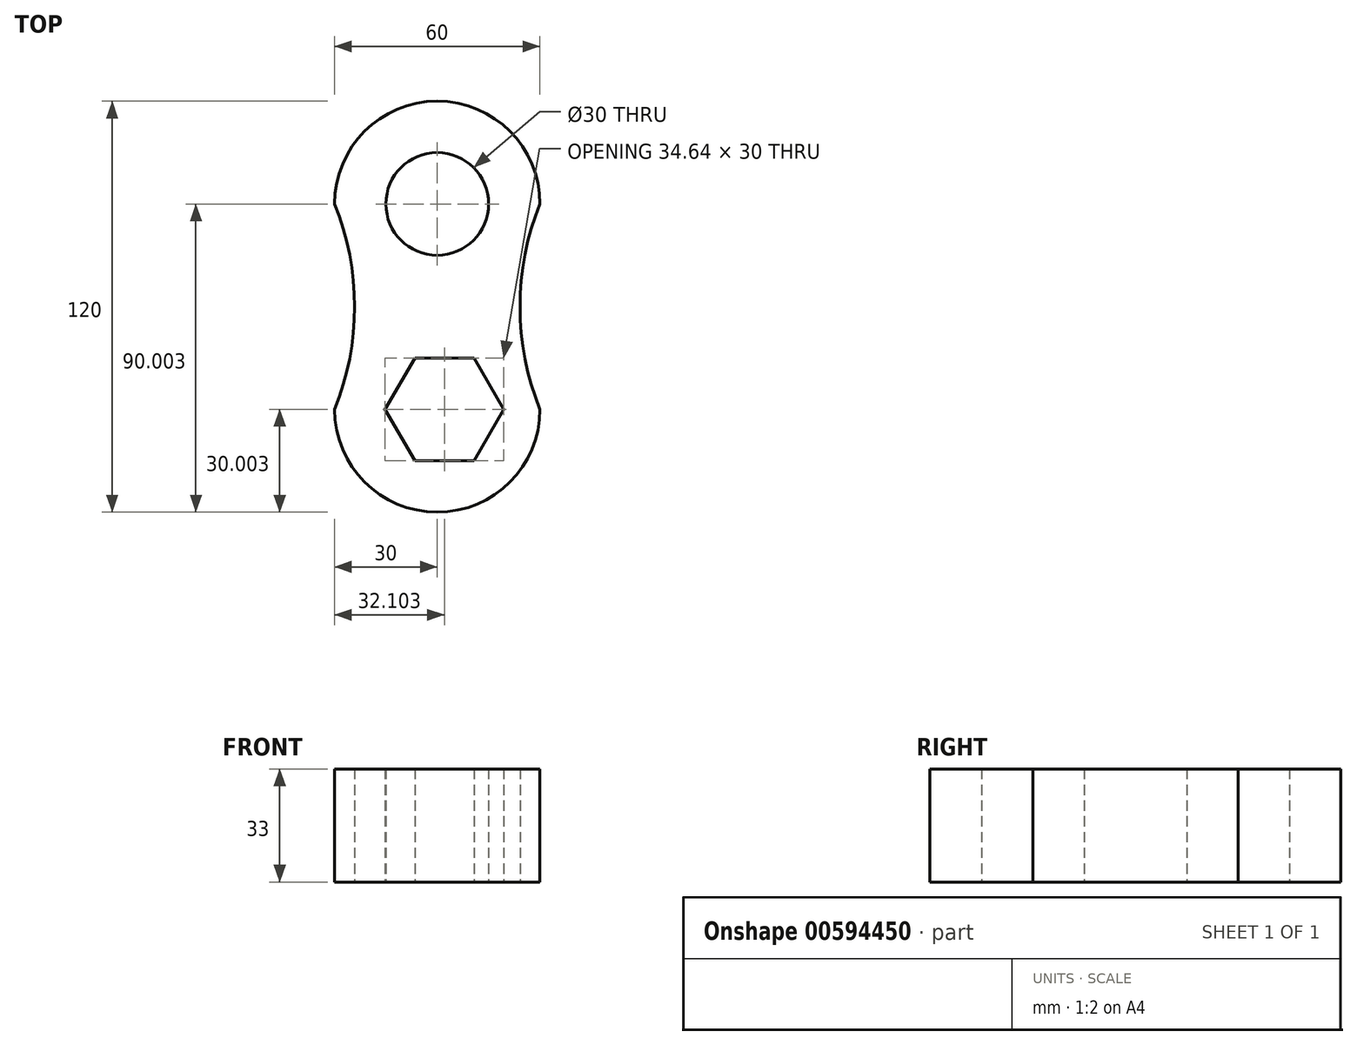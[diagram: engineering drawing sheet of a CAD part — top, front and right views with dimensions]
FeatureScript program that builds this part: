
annotation { "Feature Type Name" : "Feature", "Feature Type Description" : "" }
export const myFeature = defineFeature(function(context is Context, id is Id, definition is map)
    precondition{}
    {
        {
            var Q0;
            Q0=qCreatedBy(makeId("Top.planeOp"),FACE);
            var sketch = newSketch(context, id + "F0", { "sketchPlane" : qUnion([Q0])});
            skArc(sketch, "E0", {"start": v(-15.64, -28.34) * mm, "mid": v(14.36, -58.34) * mm, "end": v(44.36, -28.34) * mm});
            skLineSegment(sketch, "E1", {"start": v(1.46, -28.34) * mm, "end": v(-0.86, -28.34) * mm});
            skArc(sketch, "E2", {"start": v(-15.64, -28.34) * mm, "mid": v(-9.8, 1.66) * mm, "end": v(-15.64, 31.66) * mm});
            skCircle(sketch, "E3", {"center": v(14.36, 31.66) * mm, "radius": 15 * mm});
            skCircle(sketch, "E4.cCircle", {"center": v(16.46, -28.34) * mm, "radius": 15 * mm, "construction": true});
            skLineSegment(sketch, "E4.0", {"start": v(7.8, -13.34) * mm, "end": v(25.12, -13.34) * mm});
            skLineSegment(sketch, "E4.1", {"start": v(25.12, -13.34) * mm, "end": v(33.78, -28.34) * mm});
            skLineSegment(sketch, "E4.2", {"start": v(33.78, -28.34) * mm, "end": v(25.12, -43.34) * mm});
            skLineSegment(sketch, "E4.3", {"start": v(25.12, -43.34) * mm, "end": v(7.8, -43.34) * mm});
            skLineSegment(sketch, "E4.4", {"start": v(7.8, -43.34) * mm, "end": v(-0.86, -28.34) * mm});
            skLineSegment(sketch, "E4.5", {"start": v(-0.86, -28.34) * mm, "end": v(7.8, -13.34) * mm});
            skPoint(sketch, "E4.0.midPoint", {"position": v(16.46, -13.34) * mm});
            skArc(sketch, "E5", {"start": v(44.36, 31.66) * mm, "mid": v(38.52, 1.66) * mm, "end": v(44.36, -28.34) * mm});
            skArc(sketch, "E6.trimOffspring", {"start": v(44.36, 31.66) * mm, "mid": v(14.36, 61.66) * mm, "end": v(-15.64, 31.66) * mm});
            skLineSegment(sketch, "E7.trimOffspring", {"start": v(14.36, -13.34) * mm, "end": v(14.36, -13.49) * mm});
            skSolve(sketch);
        }
        {
            var Q0;
            Q0 = qSketchRegion(id + "F0", true);
            extrude(context, id + "F1", {"entities" : qUnion([Q0]), "depth" : 33 * mm, "offsetDistance" : 25 * mm});
        }
    });
